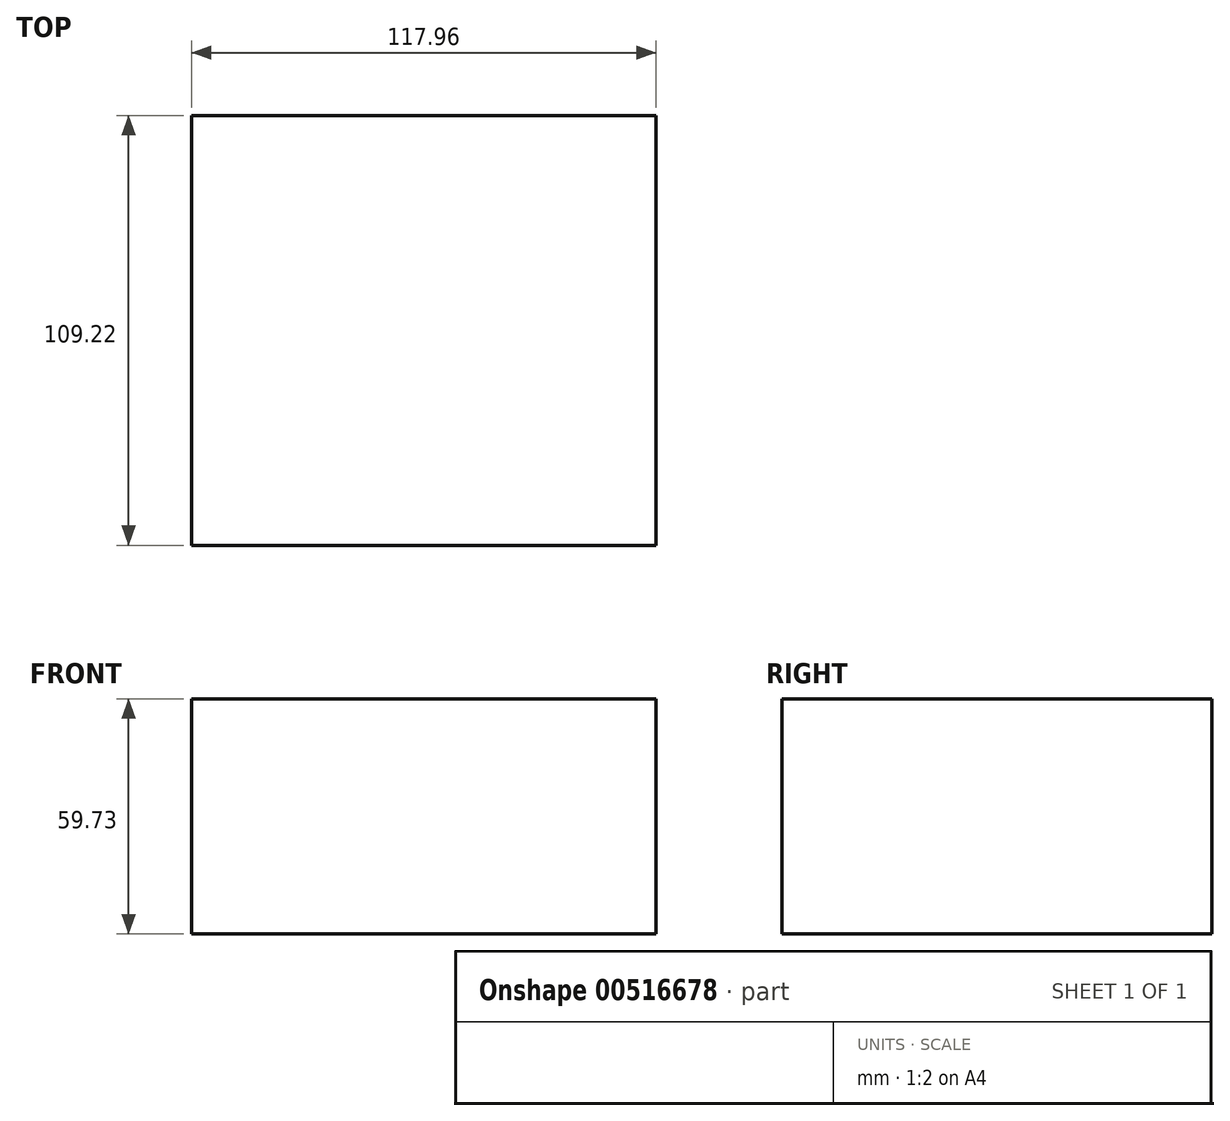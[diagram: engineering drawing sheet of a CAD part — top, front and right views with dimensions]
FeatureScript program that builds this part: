
annotation { "Feature Type Name" : "Feature", "Feature Type Description" : "" }
export const myFeature = defineFeature(function(context is Context, id is Id, definition is map)
    precondition{}
    {
        {
            var Q0;
            Q0=qCreatedBy(makeId("Front.planeOp"),FACE);
            var sketch = newSketch(context, id + "F0", { "sketchPlane" : qUnion([Q0])});
            skLineSegment(sketch, "E0.bottom", {"start": v(59.51, -47.4) * mm, "end": v(-58.45, -47.4) * mm});
            skLineSegment(sketch, "E0.top", {"start": v(59.51, 12.32) * mm, "end": v(-58.45, 12.32) * mm});
            skLineSegment(sketch, "E0.left", {"start": v(59.51, -47.4) * mm, "end": v(59.51, 12.32) * mm});
            skLineSegment(sketch, "E0.right", {"start": v(-58.45, -47.4) * mm, "end": v(-58.45, 12.32) * mm});
            skSolve(sketch);
        }
        {
            var Q0;
            Q0=makeQuery(id+"F0.imprint","IMPRINT",FACE,{"disambiguationData":[TD([[makeQuery(id+"F0.imprint","IMPRINT",EDGE,{"derivedFrom":sQuery(id+"F0.wireOp",EDGE,"E0.bottom")}),-1.0]])]});
            extrude(context, id + "F1", {"entities" : qUnion([Q0]), "depth" : 109.22 * mm, "offsetDistance" : 25.4 * mm});
        }
    });
